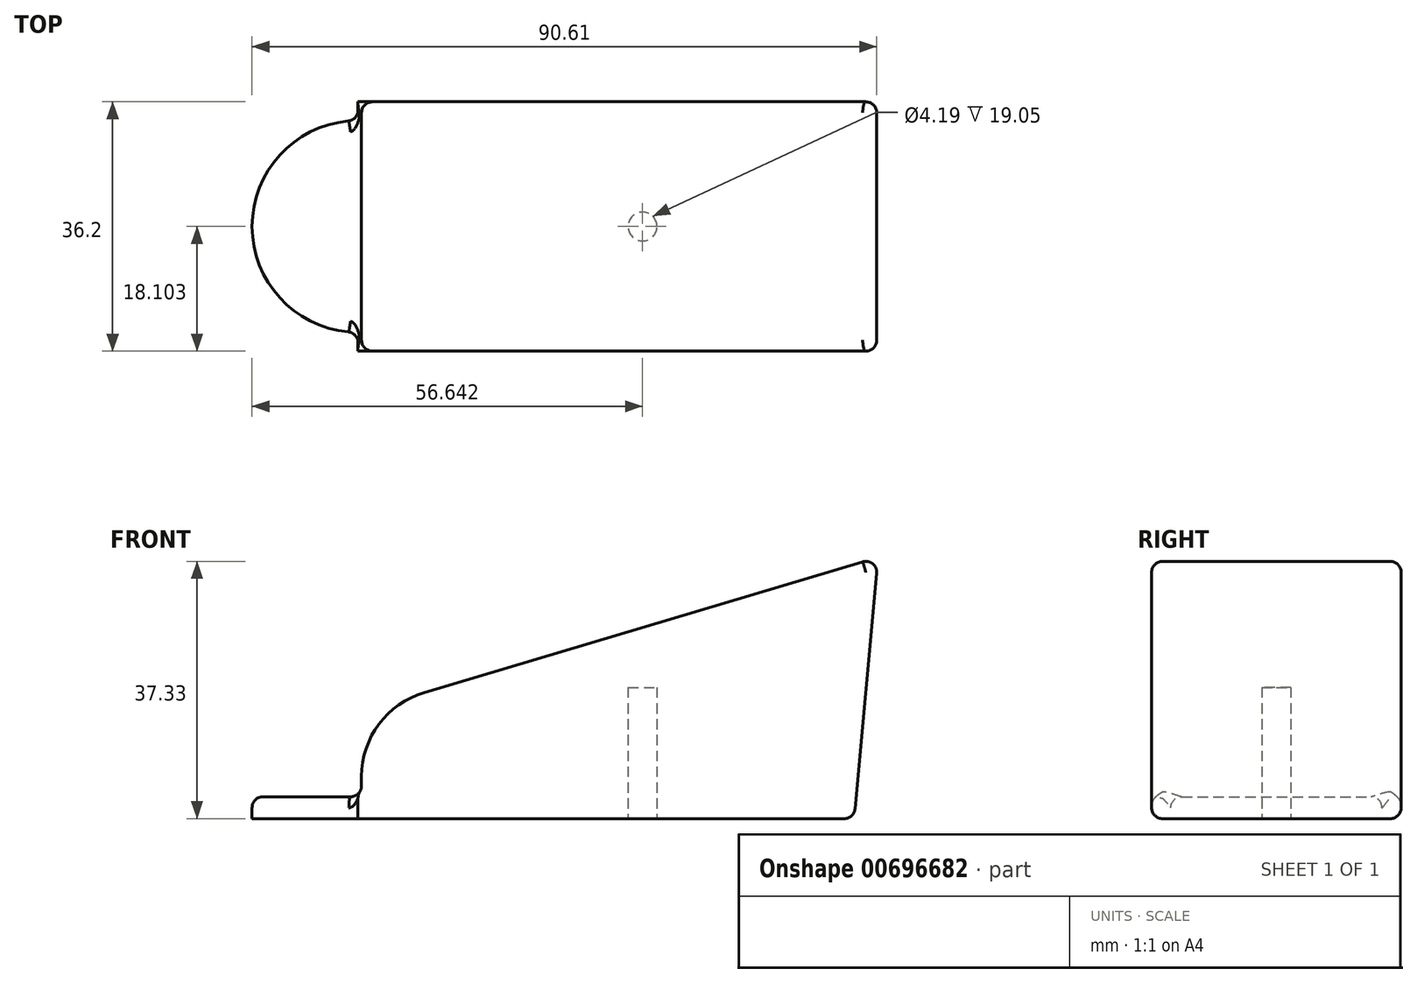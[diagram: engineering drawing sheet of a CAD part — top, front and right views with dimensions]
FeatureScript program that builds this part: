
annotation { "Feature Type Name" : "Feature", "Feature Type Description" : "" }
export const myFeature = defineFeature(function(context is Context, id is Id, definition is map)
    precondition{}
    {
        {
            var Q0;
            Q0=qCreatedBy(makeId("Front.planeOp"),FACE);
            var sketch = newSketch(context, id + "F0", { "sketchPlane" : qUnion([Q0])});
            skLineSegment(sketch, "E0", {"start": v(0, 0) * mm, "end": v(87.33, 0) * mm});
            skLineSegment(sketch, "E1", {"start": v(87.33, 0) * mm, "end": v(90.82, 37.94) * mm});
            skLineSegment(sketch, "E2", {"start": v(0, 3.18) * mm, "end": v(0, 0) * mm});
            skLineSegment(sketch, "E3", {"start": v(90.82, 37.94) * mm, "end": v(24.94, 18.29) * mm});
            skLineSegment(sketch, "E4", {"start": v(15.88, 6.12) * mm, "end": v(15.88, 3.18) * mm});
            skLineSegment(sketch, "E5", {"start": v(15.88, 3.18) * mm, "end": v(0, 3.18) * mm});
            skPoint(sketch, "E6.visualSharp", {"position": v(15.88, 15.58) * mm});
            skArc(sketch, "E6.filletArc", {"start": v(24.94, 18.29) * mm, "mid": v(18.4, 13.7) * mm, "end": v(15.88, 6.12) * mm});
            skSolve(sketch);
        }
        {
            var Q0;
            Q0 = qSketchRegion(id + "F0", true);
            extrude(context, id + "F1", {"entities" : qUnion([Q0]), "depth" : 36.2 * mm, "offsetDistance" : 25.4 * mm});
        }
        {
            var Q0;
            Q0=makeQuery(id+"F1.opExtrude","SWEPT_FACE",FACE,{"disambiguationData":[OSD([sQuery(id+"F0.wireOp",EDGE,"E0")])]});
            var sketch = newSketch(context, id + "F2", { "sketchPlane" : qUnion([Q0])});
            skLineSegment(sketch, "E7", {"start": v(0, 18.1) * mm, "end": v(81.53, 18.1) * mm, "construction": true});
            skLineSegment(sketch, "E8", {"start": v(15.37, 33.46) * mm, "end": v(15.37, 2.73) * mm, "construction": true});
            skLineSegment(sketch, "E9", {"start": v(0, 18.1) * mm, "end": v(0, 18.1) * mm});
            skPoint(sketch, "E10.visualSharp", {"position": v(0, 33.46) * mm});
            skArc(sketch, "E10.filletArc", {"start": v(15.37, 33.46) * mm, "mid": v(4.5, 28.96) * mm, "end": v(0, 18.1) * mm});
            skPoint(sketch, "E11.visualSharp", {"position": v(0, 2.73) * mm});
            skArc(sketch, "E11.filletArc", {"start": v(0, 18.1) * mm, "mid": v(4.5, 7.23) * mm, "end": v(15.37, 2.73) * mm});
            skLineSegment(sketch, "E12", {"start": v(15.37, 33.46) * mm, "end": v(15.37, 36.2) * mm});
            skLineSegment(sketch, "E13", {"start": v(15.37, 36.2) * mm, "end": v(0, 36.2) * mm});
            skLineSegment(sketch, "E14", {"start": v(0, 36.2) * mm, "end": v(0, 0) * mm});
            skLineSegment(sketch, "E15", {"start": v(0, 0) * mm, "end": v(15.37, 0) * mm});
            skLineSegment(sketch, "E16", {"start": v(15.37, 0) * mm, "end": v(15.37, 2.73) * mm});
            skSolve(sketch);
        }
        {
            var Q0;
            Q0 = qSketchRegion(id + "F2", true);
            extrude(context, id + "F3", {"entities" : qUnion([Q0]), "operationType" : NewBodyOperationType.REMOVE, "oppositeDirection" : true, "depth" : 25.4 * mm, "offsetDistance" : 25.4 * mm});
        }
        {
            var Q0;
            Q0=makeQuery(id+"F1.opExtrude","SWEPT_EDGE",EDGE,{"disambiguationData":[OSD([sQuery(id+"F0.wireOp",EDGE,"E4"),sQuery(id+"F0.wireOp",EDGE,"E5")])]});
            fillet(context, id + "F4", {"entities" : qUnion([Q0]), "radius" : 1.59 * mm, "tangentPropagation" : true, "allowEdgeOverflow" : false});
        }
        {
            var Q0;
            Q0=makeQuery(id+"F3.boolean.opBoolean","COPY",EDGE,{"derivedFrom":makeQuery(id+"F3.opExtrude","SWEPT_EDGE",EDGE,{"disambiguationData":[OSD([sQuery(id+"F2.wireOp",EDGE,"E10.filletArc"),sQuery(id+"F2.wireOp",EDGE,"E12")])]})});
            var Q1;
            Q1=makeQuery(id+"F3.boolean.opBoolean","COPY",EDGE,{"derivedFrom":makeQuery(id+"F3.opExtrude","SWEPT_EDGE",EDGE,{"disambiguationData":[OSD([sQuery(id+"F2.wireOp",EDGE,"E11.filletArc"),sQuery(id+"F2.wireOp",EDGE,"E16")])]})});
            fillet(context, id + "F5", {"entities" : qUnion([Q0, Q1]), "radius" : 1.59 * mm, "tangentPropagation" : true, "allowEdgeOverflow" : false});
        }
        {
            var Q0;
            Q0=makeQuery(id+"F1.opExtrude","SWEPT_FACE",FACE,{"disambiguationData":[OSD([sQuery(id+"F0.wireOp",EDGE,"E3")])]});
            var Q1;
            Q1=makeQuery(id+"F1.opExtrude","SWEPT_FACE",FACE,{"disambiguationData":[OSD([sQuery(id+"F0.wireOp",EDGE,"E5")])]});
            fillet(context, id + "F6", {"entities" : qUnion([Q0, Q1]), "radius" : 1.59 * mm, "tangentPropagation" : true, "allowEdgeOverflow" : false});
        }
        {
            var Q0;
            Q0=makeQuery(id+"F1.opExtrude","CAP_EDGE",EDGE,{"disambiguationData":[OSD([sQuery(id+"F0.wireOp",EDGE,"E0")])],"isStart":false});
            var Q1;
            Q1=makeQuery(id+"F3.boolean.opBoolean","COPY",EDGE,{"derivedFrom":makeQuery(id+"F3.opExtrude","SWEPT_EDGE",EDGE,{"disambiguationData":[OSD([sQuery(id+"F0.wireOp",EDGE,"E0"),sQuery(id+"F2.wireOp",EDGE,"E12"),sQuery(id+"F2.wireOp",EDGE,"E13")])]})});
            var Q2;
            Q2=makeQuery(id+"F1.opExtrude","CAP_EDGE",EDGE,{"disambiguationData":[OSD([sQuery(id+"F0.wireOp",EDGE,"E0")])],"isStart":true});
            var Q3;
            Q3=makeQuery(id+"F1.opExtrude","CAP_EDGE",EDGE,{"disambiguationData":[OSD([sQuery(id+"F0.wireOp",EDGE,"E1")])],"isStart":false});
            var Q4;
            Q4=makeQuery(id+"F1.opExtrude","CAP_EDGE",EDGE,{"disambiguationData":[OSD([sQuery(id+"F0.wireOp",EDGE,"E1")])],"isStart":true});
            var Q5;
            Q5=makeQuery(id+"F1.opExtrude","SWEPT_EDGE",EDGE,{"disambiguationData":[OSD([sQuery(id+"F0.wireOp",EDGE,"E0"),sQuery(id+"F0.wireOp",EDGE,"E1")])]});
            fillet(context, id + "F7", {"entities" : qUnion([Q0, Q1, Q2, Q3, Q4, Q5]), "radius" : 1.59 * mm, "tangentPropagation" : true, "allowEdgeOverflow" : false});
        }
        {
            var Q0;
            Q0=makeQuery(id+"F1.opExtrude","SWEPT_FACE",FACE,{"disambiguationData":[OSD([sQuery(id+"F0.wireOp",EDGE,"E0")])]});
            var sketch = newSketch(context, id + "F8", { "sketchPlane" : qUnion([Q0])});
            skLineSegment(sketch, "E17", {"start": v(0, 18.1) * mm, "end": v(78.57, 18.1) * mm, "construction": true});
            skCircle(sketch, "E18", {"center": v(15.75, 18.1) * mm, "radius": 5.08 * mm, "construction": true});
            skCircle(sketch, "E19", {"center": v(56.64, 18.1) * mm, "radius": 2.1 * mm});
            skSolve(sketch);
        }
        {
            var Q0;
            Q0=makeQuery(id+"F8.imprint","IMPRINT",FACE,{"disambiguationData":[TD([[makeQuery(id+"F8.imprint","IMPRINT",EDGE,{"derivedFrom":sQuery(id+"F8.wireOp",EDGE,"E19")}),1.0]])]});
            extrude(context, id + "F9", {"entities" : qUnion([Q0]), "operationType" : NewBodyOperationType.REMOVE, "oppositeDirection" : true, "depth" : 19.05 * mm, "offsetDistance" : 25.4 * mm});
        }
    });
